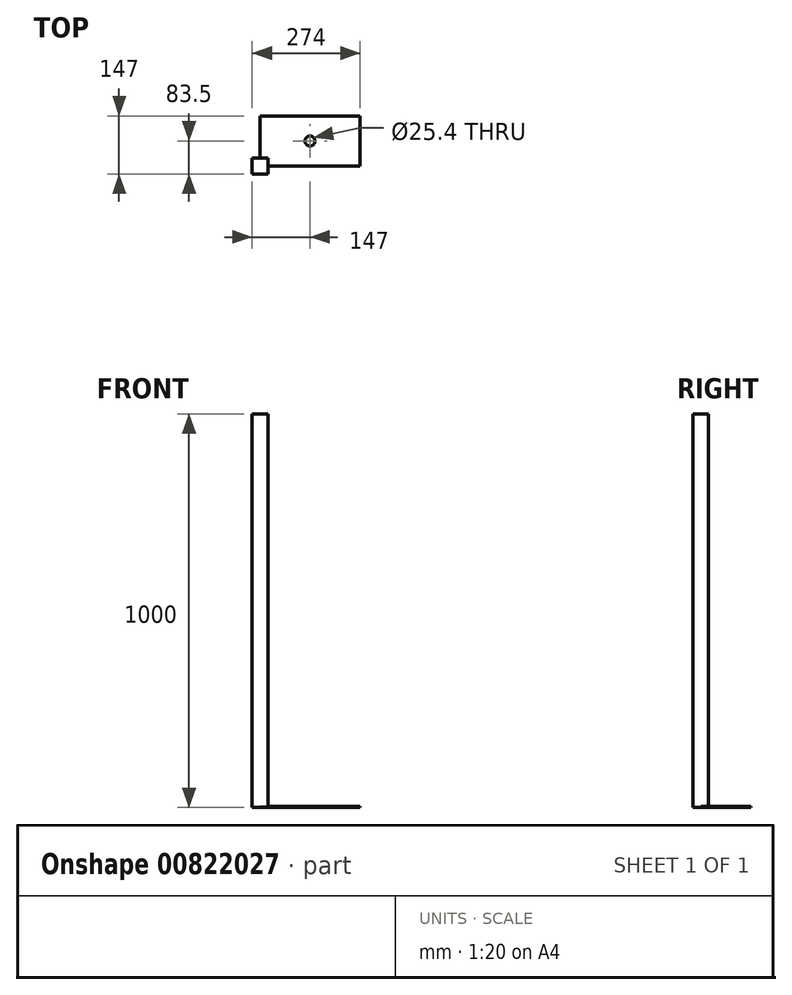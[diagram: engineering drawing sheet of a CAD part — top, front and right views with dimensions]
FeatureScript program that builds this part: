
annotation { "Feature Type Name" : "Feature", "Feature Type Description" : "" }
export const myFeature = defineFeature(function(context is Context, id is Id, definition is map)
    precondition{}
    {
        {
            var Q0;
            Q0=qCreatedBy(makeId("Top.planeOp"),FACE);
            var sketch = newSketch(context, id + "F0", { "sketchPlane" : qUnion([Q0])});
            skLineSegment(sketch, "E0.bottom", {"start": v(20, 20) * mm, "end": v(-20, 20) * mm});
            skLineSegment(sketch, "E0.top", {"start": v(20, -20) * mm, "end": v(-20, -20) * mm});
            skLineSegment(sketch, "E0.left", {"start": v(20, 20) * mm, "end": v(20, -20) * mm});
            skLineSegment(sketch, "E0.right", {"start": v(-20, 20) * mm, "end": v(-20, -20) * mm});
            skPoint(sketch, "E0.middle", {"position": v(0, 0) * mm});
            skSolve(sketch);
        }
        {
            var Q0;
            Q0=makeQuery(id+"F0.imprint","IMPRINT",FACE,{"disambiguationData":[TD([[makeQuery(id+"F0.imprint","IMPRINT",EDGE,{"derivedFrom":sQuery(id+"F0.wireOp",EDGE,"E0.bottom")}),1.0]])]});
            extrude(context, id + "F1", {"entities" : qUnion([Q0]), "depth" : 1000 * mm, "offsetDistance" : 25 * mm});
        }
        {
            var Q0;
            Q0=qCreatedBy(makeId("Top.planeOp"),FACE);
            var sketch = newSketch(context, id + "F2", { "sketchPlane" : qUnion([Q0])});
            skLineSegment(sketch, "E1.bottom", {"start": v(0, 0) * mm, "end": v(254, 0) * mm});
            skLineSegment(sketch, "E1.top", {"start": v(0, 127) * mm, "end": v(254, 127) * mm});
            skLineSegment(sketch, "E1.left", {"start": v(0, 0) * mm, "end": v(0, 127) * mm});
            skLineSegment(sketch, "E1.right", {"start": v(254, 0) * mm, "end": v(254, 127) * mm});
            skCircle(sketch, "E2", {"center": v(127, 63.5) * mm, "radius": 12.7 * mm});
            skPoint(sketch, "E2.centerSnap0", {"position": v(127, 127) * mm});
            skPoint(sketch, "E2.centerSnap1", {"position": v(0, 63.5) * mm});
            skSolve(sketch);
        }
        {
            var Q0;
            {var subQ2=sQuery(id+"F2.wireOp",EDGE,"E1.top");Q0=makeQuery(id+"F2.imprint","IMPRINT",FACE,{"disambiguationData":[TD([[makeQuery(id+"F2.imprint","IMPRINT",EDGE,{"derivedFrom":subQ2}),-1.0]])]});}
            extrude(context, id + "F3", {"entities" : qUnion([Q0]), "depth" : 0.25 * mm, "offsetDistance" : 25.4 * mm});
        }
        {
            var Q0;
            Q0 = qSketchRegion(id + "F2", true);
            extrude(context, id + "F4", {"entities" : qUnion([Q0]), "operationType" : NewBodyOperationType.ADD, "depth" : 2.54 * mm, "offsetDistance" : 25.4 * mm});
        }
    });
